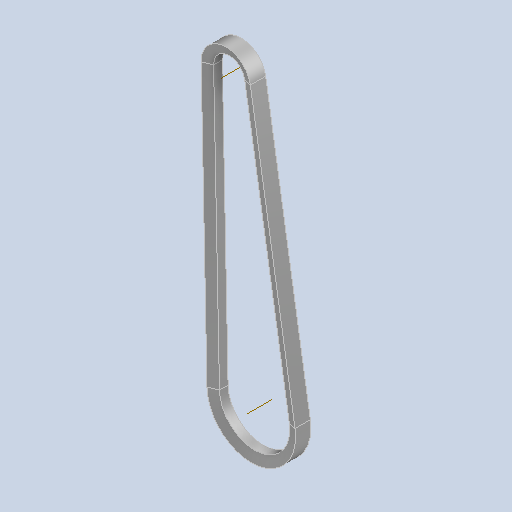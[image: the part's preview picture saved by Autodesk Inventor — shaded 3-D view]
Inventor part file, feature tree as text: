
AUTODESK INVENTOR PART (.ipt)
format: ipt  version: 2023 (Build 270158000, 158)  size: 108,544 bytes
history: native  units: mm (DEFAULTED — no unit token found)
features: other x5, sweep x1
ambient origin geometry x8: Origin, YZ Plane, XZ Plane, XY Plane, X Axis, Y Axis, Z Axis, Center Point
bodies: Solid1 (feature_tree)
feature tree (6):
  other  "Эскизная траектория"
  other  "Плоскость сечения"
  other  "РабОсь1"
  other  "РабОсь2"
  sweep  "Ремень"
  other  "Сечение"
